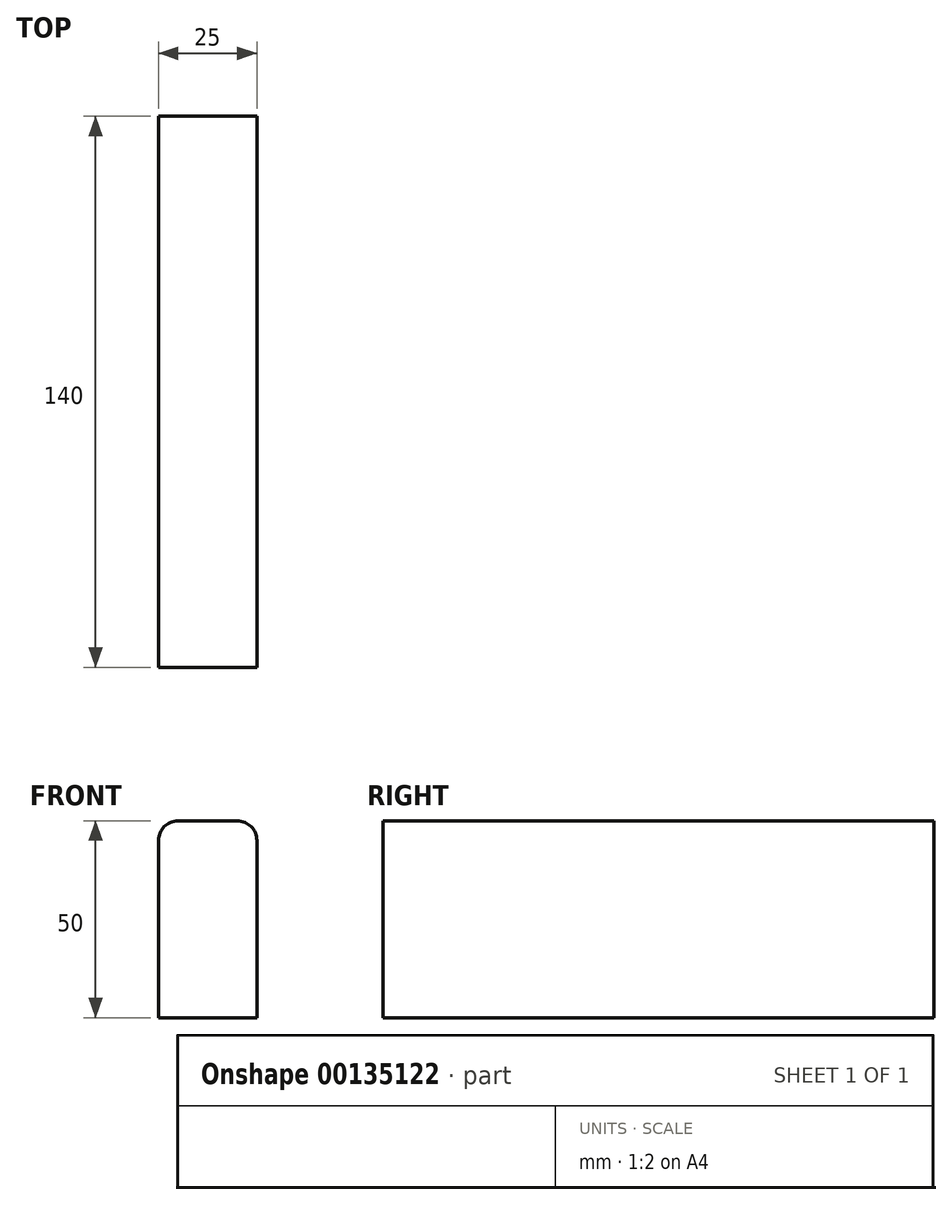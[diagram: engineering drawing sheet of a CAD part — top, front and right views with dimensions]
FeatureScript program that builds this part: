
annotation { "Feature Type Name" : "Feature", "Feature Type Description" : "" }
export const myFeature = defineFeature(function(context is Context, id is Id, definition is map)
    precondition{}
    {
        {
            var Q0;
            Q0=qCreatedBy(makeId("Front.planeOp"),FACE);
            var sketch = newSketch(context, id + "F0", { "sketchPlane" : qUnion([Q0])});
            skLineSegment(sketch, "E0.bottom", {"start": v(0, 0) * mm, "end": v(25, 0) * mm});
            skLineSegment(sketch, "E0.top", {"start": v(5, 50) * mm, "end": v(20, 50) * mm});
            skLineSegment(sketch, "E0.left", {"start": v(0, 0) * mm, "end": v(0, 45) * mm});
            skLineSegment(sketch, "E0.right", {"start": v(25, 0) * mm, "end": v(25, 45) * mm});
            skPoint(sketch, "E1.visualSharp", {"position": v(0, 50) * mm});
            skArc(sketch, "E1.filletArc", {"start": v(5, 50) * mm, "mid": v(1.46, 48.54) * mm, "end": v(0, 45) * mm});
            skPoint(sketch, "E2.visualSharp", {"position": v(25, 50) * mm});
            skArc(sketch, "E2.filletArc", {"start": v(25, 45) * mm, "mid": v(23.54, 48.54) * mm, "end": v(20, 50) * mm});
            skSolve(sketch);
        }
        {
            var Q0;
            Q0=qSketchRegion(id+"F0",true);
            extrude(context, id + "F1", {"entities" : qUnion([Q0]), "depth" : 140 * mm});
        }
    });
